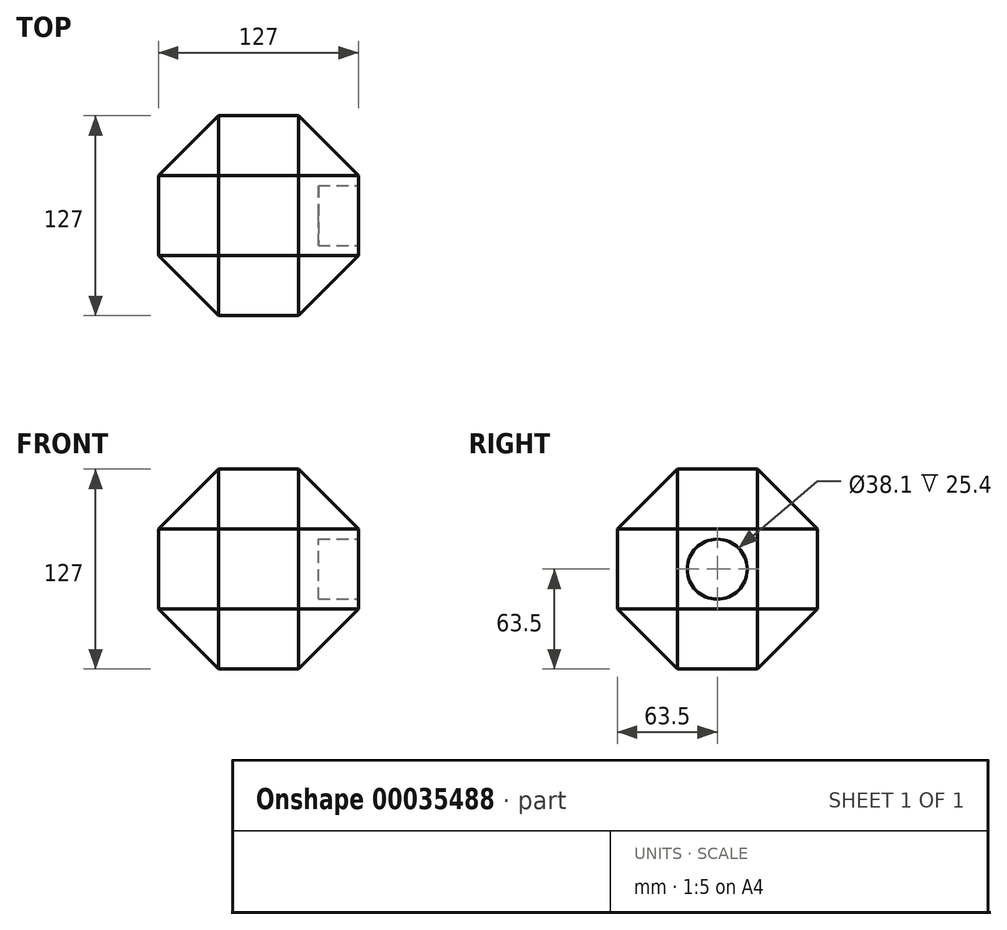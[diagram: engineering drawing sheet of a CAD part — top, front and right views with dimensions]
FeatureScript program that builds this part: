
annotation { "Feature Type Name" : "Feature", "Feature Type Description" : "" }
export const myFeature = defineFeature(function(context is Context, id is Id, definition is map)
    precondition{}
    {
        {
            var Q0;
            Q0=qCreatedBy(makeId("Top.planeOp"),FACE);
            var sketch = newSketch(context, id + "F0", { "sketchPlane" : qUnion([Q0])});
            skLineSegment(sketch, "E0.bottom", {"start": v(0, 0) * mm, "end": v(-127, 0) * mm});
            skLineSegment(sketch, "E0.top", {"start": v(0, 127) * mm, "end": v(-127, 127) * mm});
            skLineSegment(sketch, "E0.left", {"start": v(0, 0) * mm, "end": v(0, 127) * mm});
            skLineSegment(sketch, "E0.right", {"start": v(-127, 0) * mm, "end": v(-127, 127) * mm});
            skSolve(sketch);
        }
        {
            var Q0;
            Q0=makeQuery(id+"F0.imprint","IMPRINT",FACE,{"disambiguationData":[TD([[makeQuery(id+"F0.imprint","IMPRINT",EDGE,{"derivedFrom":sQuery(id+"F0.wireOp",EDGE,"E0.bottom")}),-1.0]])]});
            extrude(context, id + "F1", {"entities" : qUnion([Q0]), "depth" : 127 * mm});
        }
        {
            var Q0;
            Q0=makeQuery(id+"F1.opExtrude","SWEPT_EDGE",EDGE,{"disambiguationData":[OSD([sQuery(id+"F0.wireOp",EDGE,"E0.top"),sQuery(id+"F0.wireOp",EDGE,"E0.left")])]});
            var Q1;
            Q1=makeQuery(id+"F1.opExtrude","CAP_EDGE",EDGE,{"disambiguationData":[OSD([sQuery(id+"F0.wireOp",EDGE,"E0.left")])],"isStart":true});
            var Q2;
            Q2=makeQuery(id+"F1.opExtrude","CAP_EDGE",EDGE,{"disambiguationData":[OSD([sQuery(id+"F0.wireOp",EDGE,"E0.top")])],"isStart":true});
            var Q3;
            Q3=makeQuery(id+"F1.opExtrude","CAP_EDGE",EDGE,{"disambiguationData":[OSD([sQuery(id+"F0.wireOp",EDGE,"E0.left")])],"isStart":false});
            var Q4;
            Q4=makeQuery(id+"F1.opExtrude","CAP_EDGE",EDGE,{"disambiguationData":[OSD([sQuery(id+"F0.wireOp",EDGE,"E0.right")])],"isStart":false});
            var Q5;
            Q5=makeQuery(id+"F1.opExtrude","SWEPT_EDGE",EDGE,{"disambiguationData":[OSD([sQuery(id+"F0.wireOp",EDGE,"E0.top"),sQuery(id+"F0.wireOp",EDGE,"E0.right")])]});
            var Q6;
            Q6=makeQuery(id+"F1.opExtrude","CAP_EDGE",EDGE,{"disambiguationData":[OSD([sQuery(id+"F0.wireOp",EDGE,"E0.top")])],"isStart":false});
            var Q7;
            Q7=makeQuery(id+"F1.opExtrude","CAP_EDGE",EDGE,{"disambiguationData":[OSD([sQuery(id+"F0.wireOp",EDGE,"E0.bottom")])],"isStart":false});
            var Q8;
            Q8=makeQuery(id+"F1.opExtrude","SWEPT_EDGE",EDGE,{"disambiguationData":[OSD([sQuery(id+"F0.wireOp",EDGE,"E0.bottom"),sQuery(id+"F0.wireOp",EDGE,"E0.left")])]});
            var Q9;
            Q9=makeQuery(id+"F1.opExtrude","SWEPT_EDGE",EDGE,{"disambiguationData":[OSD([sQuery(id+"F0.wireOp",EDGE,"E0.bottom"),sQuery(id+"F0.wireOp",EDGE,"E0.right")])]});
            var Q10;
            Q10=makeQuery(id+"F1.opExtrude","CAP_EDGE",EDGE,{"disambiguationData":[OSD([sQuery(id+"F0.wireOp",EDGE,"E0.bottom")])],"isStart":true});
            var Q11;
            Q11=makeQuery(id+"F1.opExtrude","CAP_EDGE",EDGE,{"disambiguationData":[OSD([sQuery(id+"F0.wireOp",EDGE,"E0.right")])],"isStart":true});
            chamfer(context, id + "F2", {"entities" : qUnion([Q0, Q1, Q2, Q3, Q4, Q5, Q6, Q7, Q8, Q9, Q10, Q11]), "width" : 38.1 * mm, "tangentPropagation" : true});
        }
        {
            var Q0;
            Q0=makeQuery(id+"F1.opExtrude","SWEPT_FACE",FACE,{"disambiguationData":[OSD([sQuery(id+"F0.wireOp",EDGE,"E0.left")])]});
            var sketch = newSketch(context, id + "F3", { "sketchPlane" : qUnion([Q0])});
            skCircle(sketch, "E1", {"center": v(63.5, 63.5) * mm, "radius": 19.05 * mm});
            skPoint(sketch, "E1.centerSnap0", {"position": v(63.5, 88.9) * mm});
            skPoint(sketch, "E1.centerSnap1", {"position": v(38.1, 63.5) * mm});
            skSolve(sketch);
        }
        {
            var Q0;
            Q0=makeQuery(id+"F3.imprint","IMPRINT",FACE,{"disambiguationData":[TD([[makeQuery(id+"F3.imprint","IMPRINT",EDGE,{"derivedFrom":sQuery(id+"F3.wireOp",EDGE,"E1")}),1.0]])]});
            var Q1;
            Q1=sQuery(id+"F3.wireOp",EDGE,"E1");
            extrude(context, id + "F4", {"entities" : qUnion([Q0]), "operationType" : NewBodyOperationType.REMOVE, "surfaceEntities" : qUnion([Q1]), "oppositeDirection" : true, "depth" : 25.4 * mm});
        }
    });
